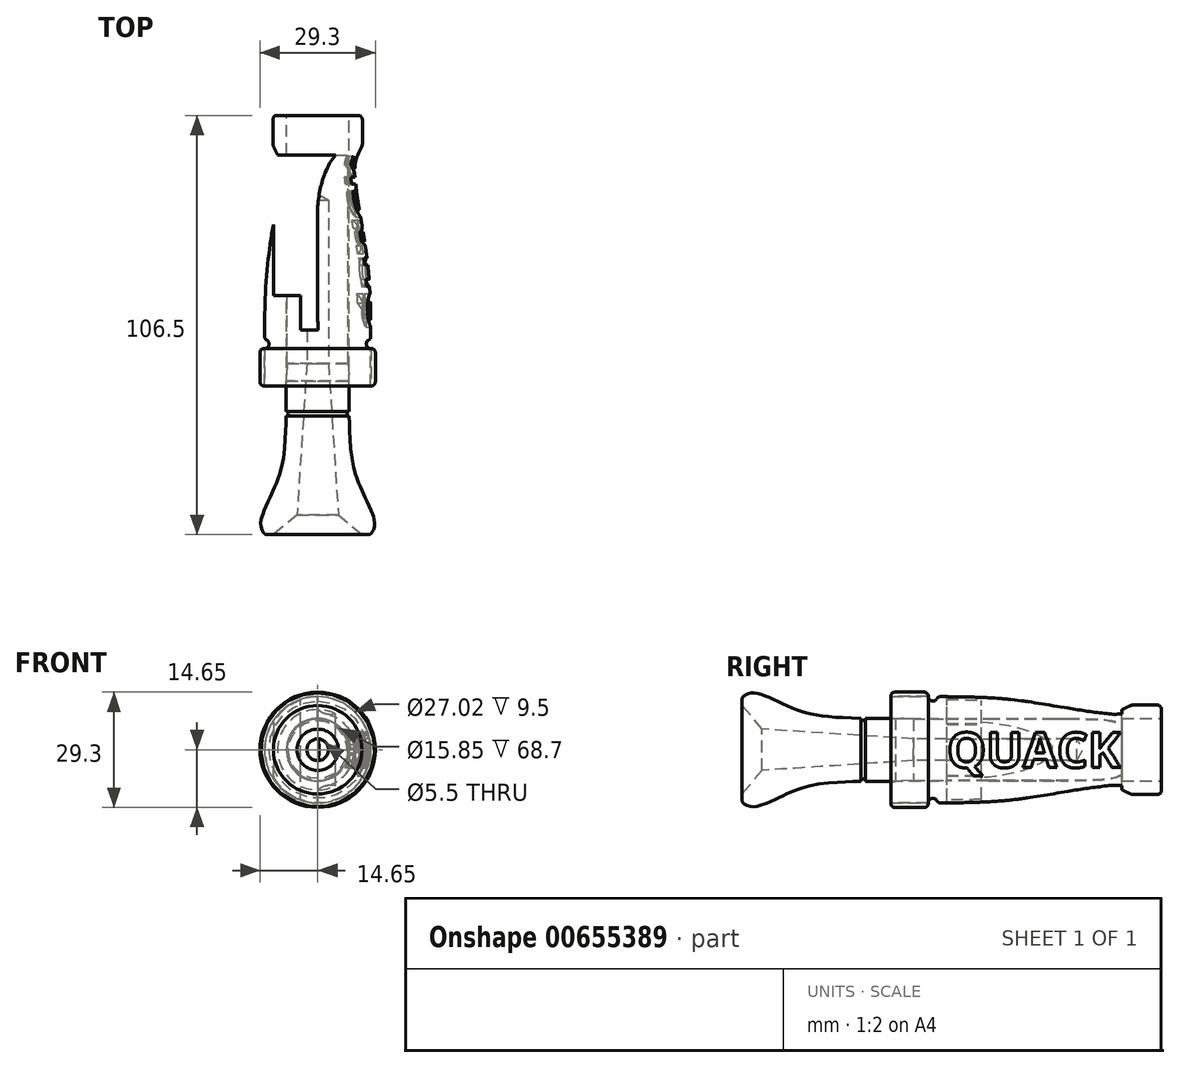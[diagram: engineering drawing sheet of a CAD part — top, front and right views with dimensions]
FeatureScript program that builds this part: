
annotation { "Feature Type Name" : "Feature", "Feature Type Description" : "" }
export const myFeature = defineFeature(function(context is Context, id is Id, definition is map)
    precondition{}
    {
        {
            var Q0;
            Q0=qCreatedBy(makeId("Top.planeOp"),FACE);
            var sketch = newSketch(context, id + "F0", { "sketchPlane" : qUnion([Q0])});
            skLineSegment(sketch, "E0", {"start": v(0, 34.01) * mm, "end": v(0, -44.14) * mm, "construction": true});
            skLineSegment(sketch, "E1", {"start": v(0, 28.73) * mm, "end": v(11.35, 28.73) * mm});
            skLineSegment(sketch, "E2", {"start": v(11.35, 28.73) * mm, "end": v(11.35, 21.23) * mm});
            skFitSpline(sketch, "E3", {"points": [v(11.35, 21.23) * mm, v(9.5, 16.23) * mm, v(12.1, -4.33) * mm, v(13.5, -28.17) * mm], "startDerivative": vector(-11.43, -29.25) * mm, "endDerivative": vector(0.17, -68.71) * mm});
            skLineSegment(sketch, "E4", {"start": v(0, -39.97) * mm, "end": v(0, 28.73) * mm});
            skArc(sketch, "E5", {"start": v(13.5, -28.17) * mm, "mid": v(12.35, -29.32) * mm, "end": v(13.5, -30.47) * mm});
            skLineSegment(sketch, "E6", {"start": v(13.5, -30.47) * mm, "end": v(13.5, -39.97) * mm});
            skLineSegment(sketch, "E7", {"start": v(13.5, -39.97) * mm, "end": v(0, -39.97) * mm});
            skSolve(sketch);
        }
        {
            var Q0;
            Q0=makeQuery(id+"F0.imprint","IMPRINT",FACE,{"disambiguationData":[TD([[makeQuery(id+"F0.imprint","IMPRINT",EDGE,{"derivedFrom":sQuery(id+"F0.wireOp",EDGE,"E1")}),-1.0]])]});
            var Q1;
            Q1=sQuery(id+"F0.wireOp",EDGE,"E0");
            revolve(context, id + "F1", {"entities" : qUnion([Q0]), "axis" : qUnion([Q1]), "revolveType" : RevolveType.FULL});
        }
        {
            var Q0;
            Q0=makeQuery(id+"F1.opRevolve","SWEPT_FACE",FACE,{"disambiguationData":[OSD([sQuery(id+"F0.wireOp",EDGE,"E1")])]});
            var sketch = newSketch(context, id + "F2", { "sketchPlane" : qUnion([Q0])});
            skCircle(sketch, "E8", {"center": v(0, 0) * mm, "radius": 7.92 * mm});
            skSolve(sketch);
        }
        {
            var Q0;
            Q0=makeQuery(id+"F2.imprint","IMPRINT",FACE,{"disambiguationData":[TD([[makeQuery(id+"F2.imprint","IMPRINT",EDGE,{"derivedFrom":sQuery(id+"F2.wireOp",EDGE,"E8")}),1.0]])]});
            extrude(context, id + "F3", {"entities" : qUnion([Q0]), "operationType" : NewBodyOperationType.REMOVE, "endBound" : BoundingType.THROUGH_ALL, "oppositeDirection" : true, "depth" : 25 * mm});
        }
        {
            var Q0;
            Q0=makeQuery(id+"F1.opRevolve","SWEPT_EDGE",EDGE,{"disambiguationData":[OSD([sQuery(id+"F0.wireOp",EDGE,"E1"),sQuery(id+"F0.wireOp",EDGE,"E2")])]});
            var Q1;
            Q1=makeQuery(id+"F1.opRevolve","SWEPT_EDGE",EDGE,{"disambiguationData":[OSD([sQuery(id+"F0.wireOp",EDGE,"E2"),sQuery(id+"F0.wireOp",EDGE,"E3")])]});
            var Q2;
            Q2=makeQuery(id+"F1.opRevolve","SWEPT_EDGE",EDGE,{"disambiguationData":[OSD([sQuery(id+"F0.wireOp",EDGE,"E3"),sQuery(id+"F0.wireOp",EDGE,"E5")])]});
            var Q3;
            Q3=makeQuery(id+"F1.opRevolve","SWEPT_EDGE",EDGE,{"disambiguationData":[OSD([sQuery(id+"F0.wireOp",EDGE,"E5"),sQuery(id+"F0.wireOp",EDGE,"E6")])]});
            var Q4;
            Q4=makeQuery(id+"F3.boolean.opBoolean","COPY",EDGE,{"derivedFrom":makeQuery(id+"F3.opExtrude","CAP_EDGE",EDGE,{"disambiguationData":[OSD([sQuery(id+"F2.wireOp",EDGE,"E8")])],"isStart":true})});
            fillet(context, id + "F4", {"entities" : qUnion([Q0, Q1, Q2, Q3, Q4]), "radius" : 1 * mm, "tangentPropagation" : true, "allowEdgeOverflow" : false});
        }
        {
            var Q0;
            Q0=qCreatedBy(makeId("Top.planeOp"),FACE);
            var sketch = newSketch(context, id + "F5", { "sketchPlane" : qUnion([Q0])});
            skLineSegment(sketch, "E9", {"start": v(0, 28.63) * mm, "end": v(0, -88.47) * mm, "construction": true});
            skLineSegment(sketch, "E10", {"start": v(0, 18.73) * mm, "end": v(7.78, 18.73) * mm});
            skLineSegment(sketch, "E11", {"start": v(0, -77.77) * mm, "end": v(13.38, -77.77) * mm});
            skLineSegment(sketch, "E12", {"start": v(7.78, 18.73) * mm, "end": v(7.78, -34.27) * mm});
            skFitSpline(sketch, "E13", {"points": [v(13.38, -77.77) * mm, v(14.03, -72.8) * mm, v(10.25, -64.12) * mm, v(8, -47.6) * mm], "startDerivative": vector(17.39, 21.88) * mm, "endDerivative": vector(-1.44, 59.8) * mm});
            skLineSegment(sketch, "E14", {"start": v(-21.94, -39.77) * mm, "end": v(21.19, -39.77) * mm, "construction": true});
            skArc(sketch, "E15", {"start": v(8, -46.45) * mm, "mid": v(7.43, -47.02) * mm, "end": v(8, -47.6) * mm});
            skLineSegment(sketch, "E16", {"start": v(7.78, -34.27) * mm, "end": v(8, -38.77) * mm});
            skLineSegment(sketch, "E17", {"start": v(8, -38.77) * mm, "end": v(8, -46.45) * mm});
            skLineSegment(sketch, "E18", {"start": v(0, 18.73) * mm, "end": v(0, -77.77) * mm});
            skPoint(sketch, "E19", {"position": v(0, -77.77) * mm});
            skSolve(sketch);
        }
        {
            var Q0;
            Q0=qSketchRegion(id+"F5",true);
            var Q1;
            Q1=sQuery(id+"F5.wireOp",EDGE,"E18");
            revolve(context, id + "F6", {"entities" : qUnion([Q0]), "axis" : qUnion([Q1]), "revolveType" : RevolveType.FULL});
        }
        {
            var Q0;
            Q0=makeQuery(id+"F6.opRevolve","SWEPT_FACE",FACE,{"disambiguationData":[OSD([sQuery(id+"F5.wireOp",EDGE,"E11")])]});
            var sketch = newSketch(context, id + "F7", { "sketchPlane" : qUnion([Q0])});
            skPoint(sketch, "E20", {"position": v(0, 0) * mm});
            skSolve(sketch);
        }
        {
            var Q0;
            Q0=sQuery(id+"F7.wireOp",VERTEX,"E20");
            var Q1;
            Q1=makeQuery(id+"F6.opRevolve","SWEPT_BODY",BODY,{"disambiguationData":[OSD([sQuery(id+"F5.wireOp",EDGE,"E10"),sQuery(id+"F5.wireOp",EDGE,"E11"),sQuery(id+"F5.wireOp",EDGE,"E12"),sQuery(id+"F5.wireOp",EDGE,"E13"),sQuery(id+"F5.wireOp",EDGE,"E15"),sQuery(id+"F5.wireOp",EDGE,"E16"),sQuery(id+"F5.wireOp",EDGE,"E17"),sQuery(id+"F5.wireOp",EDGE,"E18")])]});
            hole(context, id + "F8", {"style" : HoleStyle.SIMPLE, "holeDiameter" : 5.5 * mm, "endStyle" : HoleEndStyle.BLIND, "holeDepth" : 85 * mm, "locations" : qUnion([Q0]), "scope" : qUnion([Q1])});
        }
        {
            var Q0;
            Q0=qCreatedBy(makeId("Top.planeOp"),FACE);
            var sketch = newSketch(context, id + "F9", { "sketchPlane" : qUnion([Q0])});
            skLineSegment(sketch, "E21", {"start": v(0, 26.5) * mm, "end": v(0, -88.94) * mm, "construction": true});
            skLineSegment(sketch, "E22.0", {"start": v(0, -77.77) * mm, "end": v(11.25, -77.77) * mm});
            skLineSegment(sketch, "E23", {"start": v(11.25, -77.77) * mm, "end": v(5.25, -72.77) * mm});
            skLineSegment(sketch, "E24", {"start": v(5.25, -72.77) * mm, "end": v(2.75, -34.27) * mm});
            skLineSegment(sketch, "E25", {"start": v(2.75, -34.27) * mm, "end": v(0, -34.27) * mm});
            skLineSegment(sketch, "E26", {"start": v(0, -34.27) * mm, "end": v(0, -77.77) * mm});
            skPoint(sketch, "E27.orphan", {"position": v(-13.37, -77.77) * mm});
            skPoint(sketch, "E28.orphan", {"position": v(13.38, -77.77) * mm});
            skSolve(sketch);
        }
        {
            var Q0;
            Q0=qSketchRegion(id+"F9",true);
            var Q1;
            Q1=sQuery(id+"F9.wireOp",EDGE,"E26");
            revolve(context, id + "F10", {"operationType" : NewBodyOperationType.REMOVE, "entities" : qUnion([Q0]), "axis" : qUnion([Q1]), "revolveType" : RevolveType.FULL, "oppositeDirection" : true});
        }
        {
            var Q0;
            Q0=makeQuery(id+"F10.boolean.opBoolean","COPY",EDGE,{"derivedFrom":makeQuery(id+"F10.opRevolve","SWEPT_EDGE",EDGE,{"disambiguationData":[OSD([sQuery(id+"F9.wireOp",EDGE,"E22.0"),sQuery(id+"F9.wireOp",EDGE,"E23")])]})});
            var Q1;
            Q1=makeQuery(id+"F6.opRevolve","SWEPT_EDGE",EDGE,{"disambiguationData":[OSD([sQuery(id+"F5.wireOp",EDGE,"E11"),sQuery(id+"F5.wireOp",EDGE,"E13")])]});
            fillet(context, id + "F11", {"entities" : qUnion([Q0, Q1]), "radius" : 1 * mm, "tangentPropagation" : true, "allowEdgeOverflow" : false});
        }
        {
            var Q0;
            Q0=qCreatedBy(makeId("Top.planeOp"),FACE);
            var sketch = newSketch(context, id + "F12", { "sketchPlane" : qUnion([Q0])});
            skLineSegment(sketch, "E29", {"start": v(0.05, -25.77) * mm, "end": v(-4.3, -25.77) * mm});
            skLineSegment(sketch, "E30", {"start": v(-4.3, -25.77) * mm, "end": v(-4.3, -17.02) * mm});
            skLineSegment(sketch, "E31", {"start": v(-4.3, -17.02) * mm, "end": v(-11.23, -17.02) * mm});
            skLineSegment(sketch, "E32", {"start": v(-11.23, -17.02) * mm, "end": v(-11.23, 18.73) * mm});
            skLineSegment(sketch, "E33.0", {"start": v(-7.78, 18.73) * mm, "end": v(4.53, 18.73) * mm});
            skFitSpline(sketch, "E34", {"points": [v(-0.08, 0.73) * mm, v(4.53, 18.73) * mm], "startDerivative": vector(-0.06, 12.7) * mm, "endDerivative": vector(14.01, 17.84) * mm});
            skPoint(sketch, "E35.orphan", {"position": v(7.78, 18.73) * mm});
            skLineSegment(sketch, "E36.trimOffspring", {"start": v(-0.08, 0.73) * mm, "end": v(0.05, -25.77) * mm});
            skLineSegment(sketch, "E37", {"start": v(4.53, 18.73) * mm, "end": v(-11.23, 18.73) * mm});
            skSolve(sketch);
        }
        {
            var Q0;
            Q0=makeQuery(id+"F12.imprint","IMPRINT",FACE,{"disambiguationData":[TD([[makeQuery(id+"F12.imprint","IMPRINT",EDGE,{"derivedFrom":sQuery(id+"F12.wireOp",EDGE,"E29")}),-1.0]])]});
            extrude(context, id + "F13", {"entities" : qUnion([Q0]), "operationType" : NewBodyOperationType.REMOVE, "endBound" : BoundingType.THROUGH_ALL, "oppositeDirection" : true, "depth" : 25 * mm, "hasSecondDirection" : true, "secondDirectionBound" : SecondDirectionBoundingType.THROUGH_ALL, "secondDirectionOppositeDirection" : false, "secondDirectionDepth" : 25 * mm, "offsetDistance" : 25 * mm});
        }
        {
            var Q0;
            Q0=makeQuery(id+"F1.opRevolve","SWEPT_FACE",FACE,{"disambiguationData":[OSD([sQuery(id+"F0.wireOp",EDGE,"E7")])]});
            var sketch = newSketch(context, id + "F14", { "sketchPlane" : qUnion([Q0])});
            skCircle(sketch, "E38.0", {"center": v(0, 0) * mm, "radius": 13.51 * mm});
            skCircle(sketch, "E39", {"center": v(0, 0) * mm, "radius": 14.65 * mm});
            skSolve(sketch);
        }
        {
            var Q0;
            Q0=qSketchRegion(id+"F14",true);
            extrude(context, id + "F15", {"entities" : qUnion([Q0]), "oppositeDirection" : true, "depth" : 9.5 * mm});
        }
        {
            var Q0;
            Q0=makeQuery(id+"F15.opExtrude","CAP_EDGE",EDGE,{"disambiguationData":[OSD([sQuery(id+"F14.wireOp",EDGE,"E39")])],"isStart":true});
            var Q1;
            Q1=makeQuery(id+"F15.opExtrude","CAP_EDGE",EDGE,{"disambiguationData":[OSD([sQuery(id+"F14.wireOp",EDGE,"E39")])],"isStart":false});
            fillet(context, id + "F16", {"entities" : qUnion([Q0, Q1]), "radius" : 1 * mm, "tangentPropagation" : true, "allowEdgeOverflow" : false});
        }
        {
            var Q0;
            Q0=qCreatedBy(makeId("Top.planeOp"),FACE);
            var sketch = newSketch(context, id + "F17", { "sketchPlane" : qUnion([Q0])});
            skLineSegment(sketch, "E40.0", {"start": v(0, 34.01) * mm, "end": v(0, -44.14) * mm});
            skLineSegment(sketch, "E40.4", {"start": v(0, -39.97) * mm, "end": v(0, 28.73) * mm});
            skLineSegment(sketch, "E41", {"start": v(10, 21.23) * mm, "end": v(0, 21.23) * mm});
            skLineSegment(sketch, "E42", {"start": v(12.25, -28.17) * mm, "end": v(0, -28.17) * mm});
            skFitSpline(sketch, "E43.0", {"points": [v(10.19, 21.68) * mm, v(9.97, 21.13) * mm, v(9.62, 20.42) * mm, v(9.15, 19.46) * mm, v(8.8, 18.66) * mm, v(8.5, 17.76) * mm, v(8.28, 16.72) * mm, v(8.18, 15.53) * mm, v(8.17, 14.22) * mm, v(8.25, 12.78) * mm, v(8.44, 10.71) * mm, v(8.82, 7.88) * mm, v(9.42, 4.22) * mm, v(9.97, 1.07) * mm, v(10.39, -1.43) * mm, v(10.69, -3.28) * mm, v(10.96, -5.07) * mm, v(11.27, -7.4) * mm, v(11.6, -10.19) * mm, v(11.87, -13.49) * mm, v(12.06, -16.82) * mm, v(12.21, -21.47) * mm, v(12.24, -25.31) * mm, v(12.25, -28.17) * mm, v(10.19, 21.68) * mm]});
            skFitSpline(sketch, "E44.0", {"points": [v(10.19, 21.68) * mm, v(9.97, 21.13) * mm, v(9.62, 20.42) * mm, v(9.15, 19.46) * mm, v(8.8, 18.66) * mm, v(8.5, 17.76) * mm, v(8.28, 16.72) * mm, v(8.18, 15.53) * mm, v(8.17, 14.22) * mm, v(8.25, 12.78) * mm, v(8.44, 10.71) * mm, v(8.82, 7.88) * mm, v(9.42, 4.22) * mm, v(9.97, 1.07) * mm, v(10.39, -1.43) * mm, v(10.69, -3.28) * mm, v(10.96, -5.07) * mm, v(11.27, -7.4) * mm, v(11.6, -10.19) * mm, v(11.87, -13.49) * mm, v(12.06, -16.82) * mm, v(12.21, -21.47) * mm, v(12.24, -25.31) * mm, v(12.25, -28.17) * mm]});
            skSolve(sketch);
        }
        {
            var Q0;
            Q0=qSketchRegion(id+"F17",true);
            var Q1;
            Q1=sQuery(id+"F17.wireOp",EDGE,"E44.0");
            var Q2;
            Q2=sQuery(id+"F17.wireOp",EDGE,"E40.4");
            revolve(context, id + "F18", {"bodyType" : ToolBodyType.SURFACE, "entities" : qUnion([Q0]), "surfaceEntities" : qUnion([Q1]), "axis" : qUnion([Q2]), "revolveType" : RevolveType.FULL});
        }
        {
            var Q0;
            Q0=qCreatedBy(makeId("Right.planeOp"),FACE);
            cPlane(context, id + "F19", {"entities" : qUnion([Q0]), "cplaneType" : CPlaneType.OFFSET, "offset" : 15 * mm, "width" : 150 * mm, "height" : 150 * mm});
        }
        {
            var Q0;
            Q0=qCreatedBy(id+"F19.planeOp",FACE);
            var sketch = newSketch(context, id + "F20", { "sketchPlane" : qUnion([Q0])});
            skText(sketch, "E45", { "text": "QUACK", "fontName": "OpenSans-Bold.ttf"});
            const initialGuessF20  = {"E45": [-0.0257, -0.00454, 1, 0, 0.00896]};
            skSetInitialGuess(sketch, initialGuessF20);
            skSolve(sketch);
        }
        {
            var Q0;
            Q0=qSketchRegion(id+"F20",true);
            var Q1;
            Q1=makeQuery(id+"F18.opRevolve","SWEPT_FACE",FACE,{"disambiguationData":[OSD([sQuery(id+"F17.wireOp",EDGE,"E44.0")])]});
            var Q2;
            Q2=makeQuery(id+"F18.opRevolve","SWEPT_FACE",FACE,{"disambiguationData":[OSD([sQuery(id+"F17.wireOp",EDGE,"E44.0")])]});
            extrude(context, id + "F21", {"entities" : qUnion([Q0]), "operationType" : NewBodyOperationType.REMOVE, "endBound" : BoundingType.UP_TO_SURFACE, "oppositeDirection" : true, "endBoundEntityFace" : qUnion([Q1]), "depth" : 25 * mm});
        }
    });
